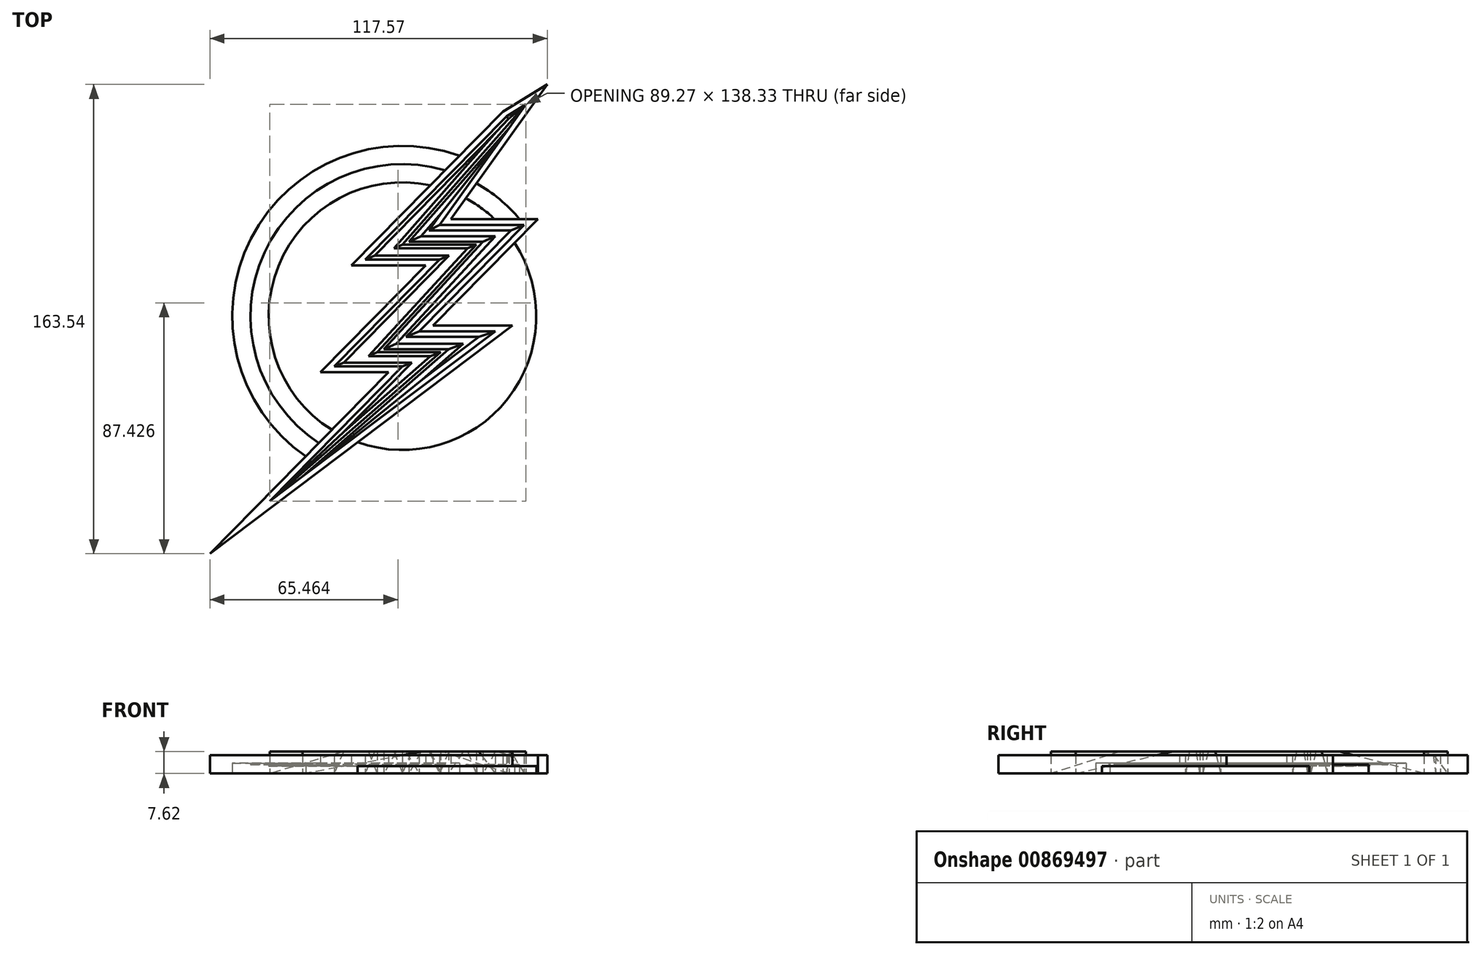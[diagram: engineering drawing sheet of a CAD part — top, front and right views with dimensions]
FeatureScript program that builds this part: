
annotation { "Feature Type Name" : "Feature", "Feature Type Description" : "" }
export const myFeature = defineFeature(function(context is Context, id is Id, definition is map)
    precondition{}
    {
        {
            var Q0;
            Q0=qCreatedBy(makeId("Top.planeOp"),FACE);
            var sketch = newSketch(context, id + "F0", { "sketchPlane" : qUnion([Q0])});
            skCircle(sketch, "E0", {"center": v(0, 0) * mm, "radius": 46.64 * mm});
            skCircle(sketch, "E1.0", {"center": v(0, 0) * mm, "radius": 53 * mm});
            skCircle(sketch, "E2.0", {"center": v(0, 0) * mm, "radius": 59.34 * mm});
            skLineSegment(sketch, "E3", {"start": v(36.25, 69.68) * mm, "end": v(-12.96, 19.72) * mm});
            skLineSegment(sketch, "E4", {"start": v(-12.96, 19.72) * mm, "end": v(12.96, 19.72) * mm});
            skLineSegment(sketch, "E5", {"start": v(12.96, 19.72) * mm, "end": v(-23.75, -17.55) * mm});
            skLineSegment(sketch, "E6", {"start": v(-23.75, -17.55) * mm, "end": v(0, -17.55) * mm});
            skLineSegment(sketch, "E7", {"start": v(0, -17.55) * mm, "end": v(-46.26, -64.52) * mm});
            skLineSegment(sketch, "E8", {"start": v(-46.26, -64.52) * mm, "end": v(24.6, -11.08) * mm});
            skLineSegment(sketch, "E9", {"start": v(24.6, -11.08) * mm, "end": v(32.28, -5.3) * mm});
            skLineSegment(sketch, "E10", {"start": v(32.28, -5.3) * mm, "end": v(5.82, -5.3) * mm});
            skLineSegment(sketch, "E11", {"start": v(5.82, -5.3) * mm, "end": v(37.86, 27.24) * mm});
            skLineSegment(sketch, "E12", {"start": v(37.86, 27.24) * mm, "end": v(42.38, 31.82) * mm});
            skLineSegment(sketch, "E13", {"start": v(42.38, 31.82) * mm, "end": v(12.96, 31.82) * mm});
            skLineSegment(sketch, "E14", {"start": v(12.96, 31.82) * mm, "end": v(43.01, 73.81) * mm});
            skLineSegment(sketch, "E15", {"start": v(43.01, 73.81) * mm, "end": v(36.25, 69.68) * mm});
            skLineSegment(sketch, "E16", {"start": v(-46.26, -64.52) * mm, "end": v(13.33, -12.58) * mm});
            skLineSegment(sketch, "E17", {"start": v(13.33, -12.58) * mm, "end": v(-8.83, -12.58) * mm});
            skLineSegment(sketch, "E18", {"start": v(-8.83, -12.58) * mm, "end": v(25.73, 24.98) * mm});
            skLineSegment(sketch, "E19", {"start": v(25.73, 24.98) * mm, "end": v(0, 24.98) * mm});
            skLineSegment(sketch, "E20", {"start": v(0, 24.98) * mm, "end": v(43.01, 73.81) * mm});
            skLineSegment(sketch, "E21", {"start": v(13.33, -12.58) * mm, "end": v(32.28, -5.3) * mm});
            skLineSegment(sketch, "E22", {"start": v(-8.83, -12.58) * mm, "end": v(-23.75, -17.55) * mm});
            skLineSegment(sketch, "E23", {"start": v(13.33, -12.58) * mm, "end": v(0, -17.55) * mm});
            skLineSegment(sketch, "E24", {"start": v(25.73, 24.98) * mm, "end": v(12.96, 19.72) * mm});
            skLineSegment(sketch, "E25", {"start": v(25.73, 24.98) * mm, "end": v(42.38, 31.82) * mm});
            skLineSegment(sketch, "E26", {"start": v(12.96, 31.82) * mm, "end": v(0, 24.98) * mm});
            skLineSegment(sketch, "E27", {"start": v(0, 24.98) * mm, "end": v(-12.96, 19.72) * mm});
            skLineSegment(sketch, "E28.0", {"start": v(50.48, 80.76) * mm, "end": v(34.98, 71.28) * mm});
            skLineSegment(sketch, "E28.1", {"start": v(16.91, 33.85) * mm, "end": v(50.48, 80.76) * mm});
            skLineSegment(sketch, "E28.2", {"start": v(-4.85, -19.59) * mm, "end": v(-67.1, -82.78) * mm});
            skLineSegment(sketch, "E28.3", {"start": v(-28.6, -19.59) * mm, "end": v(-4.85, -19.59) * mm});
            skLineSegment(sketch, "E28.4", {"start": v(8.1, 17.69) * mm, "end": v(-28.6, -19.59) * mm});
            skLineSegment(sketch, "E28.5", {"start": v(-17.81, 17.69) * mm, "end": v(8.1, 17.69) * mm});
            skLineSegment(sketch, "E28.6", {"start": v(-67.1, -82.78) * mm, "end": v(25.83, -12.7) * mm});
            skLineSegment(sketch, "E28.7", {"start": v(25.83, -12.7) * mm, "end": v(38.35, -3.26) * mm});
            skLineSegment(sketch, "E28.8", {"start": v(34.98, 71.28) * mm, "end": v(-17.81, 17.69) * mm});
            skLineSegment(sketch, "E28.9", {"start": v(38.35, -3.26) * mm, "end": v(10.68, -3.26) * mm});
            skLineSegment(sketch, "E28.10", {"start": v(10.68, -3.26) * mm, "end": v(39.31, 25.81) * mm});
            skLineSegment(sketch, "E28.11", {"start": v(39.31, 25.81) * mm, "end": v(47.23, 33.85) * mm});
            skLineSegment(sketch, "E28.12", {"start": v(47.23, 33.85) * mm, "end": v(16.91, 33.85) * mm});
            skLineSegment(sketch, "E29.0", {"start": v(2.25, 26) * mm, "end": v(43.77, 73.14) * mm});
            skLineSegment(sketch, "E29.1", {"start": v(-45.6, -65.29) * mm, "end": v(16.05, -11.57) * mm});
            skLineSegment(sketch, "E29.2", {"start": v(16.05, -11.57) * mm, "end": v(-6.51, -11.57) * mm});
            skLineSegment(sketch, "E29.3", {"start": v(-6.51, -11.57) * mm, "end": v(28.05, 26) * mm});
            skLineSegment(sketch, "E29.4", {"start": v(28.05, 26) * mm, "end": v(2.25, 26) * mm});
            skSolve(sketch);
        }
        {
            var Q0;
            {var subQ0=sQuery(id+"F0.wireOp",EDGE,"E9");Q0=makeQuery(id+"F0.imprint","IMPRINT",FACE,{"disambiguationData":[TD([[makeQuery(id+"F0.imprint","IMPRINT",EDGE,{"derivedFrom":subQ0}),-1.0]])]});}
            var Q1;
            {var subQ0=sQuery(id+"F0.wireOp",EDGE,"E4");Q1=makeQuery(id+"F0.imprint","IMPRINT",FACE,{"disambiguationData":[TD([[makeQuery(id+"F0.imprint","IMPRINT",EDGE,{"derivedFrom":subQ0}),-1.0]])]});}
            var Q2;
            {var subQ0=sQuery(id+"F0.wireOp",EDGE,"E13");var subQ1=sQuery(id+"F0.wireOp",EDGE,"E0");var subQ2=makeQuery(id+"F0.imprint","INTERSECT",VERTEX,{"derivedFrom":[subQ1,subQ0]});Q2=makeQuery(id+"F0.imprint","IMPRINT",FACE,{"disambiguationData":[TD([[makeQuery(id+"F0.imprint","IMPRINT",EDGE,{"disambiguationData":[TD([[subQ2,-1.0]])],"derivedFrom":subQ1}),1.0]])]});}
            extrude(context, id + "F1", {"entities" : qUnion([Q0, Q1, Q2]), "depth" : 5.08 * mm, "offsetDistance" : 25.4 * mm});
        }
        {
            var Q0;
            {var subQ11=sQuery(id+"F0.wireOp",EDGE,"E4");Q0=makeQuery(id+"F0.imprint","IMPRINT",FACE,{"disambiguationData":[TD([[makeQuery(id+"F0.imprint","IMPRINT",EDGE,{"derivedFrom":subQ11}),-1.0]])]});}
            var Q1;
            {var subQ0=sQuery(id+"F0.wireOp",EDGE,"E9");Q1=makeQuery(id+"F0.imprint","IMPRINT",FACE,{"disambiguationData":[TD([[makeQuery(id+"F0.imprint","IMPRINT",EDGE,{"derivedFrom":subQ0}),-1.0]])]});}
            var Q2;
            {var subQ0=sQuery(id+"F0.wireOp",EDGE,"E8");var subQ1=sQuery(id+"F0.wireOp",EDGE,"E0");var subQ2=makeQuery(id+"F0.imprint","INTERSECT",VERTEX,{"derivedFrom":[subQ1,subQ0]});Q2=makeQuery(id+"F0.imprint","IMPRINT",FACE,{"disambiguationData":[TD([[makeQuery(id+"F0.imprint","IMPRINT",EDGE,{"disambiguationData":[TD([[subQ2,-1.0]])],"derivedFrom":subQ1}),-1.0]])]});}
            var Q3;
            {var subQ0=sQuery(id+"F0.wireOp",EDGE,"E28.2");var subQ1=sQuery(id+"F0.wireOp",EDGE,"E0");var subQ2=makeQuery(id+"F0.imprint","INTERSECT",VERTEX,{"derivedFrom":[subQ1,subQ0]});Q3=makeQuery(id+"F0.imprint","IMPRINT",FACE,{"disambiguationData":[TD([[makeQuery(id+"F0.imprint","IMPRINT",EDGE,{"disambiguationData":[TD([[subQ2,-1.0]])],"derivedFrom":subQ1}),-1.0]])]});}
            var Q4;
            {var subQ0=sQuery(id+"F0.wireOp",EDGE,"E28.2");var subQ1=sQuery(id+"F0.wireOp",EDGE,"E1.0");var subQ2=makeQuery(id+"F0.imprint","INTERSECT",VERTEX,{"derivedFrom":[subQ1,subQ0]});Q4=makeQuery(id+"F0.imprint","IMPRINT",FACE,{"disambiguationData":[TD([[makeQuery(id+"F0.imprint","IMPRINT",EDGE,{"disambiguationData":[TD([[subQ2,-1.0]])],"derivedFrom":subQ1}),-1.0]])]});}
            var Q5;
            {var subQ0=sQuery(id+"F0.wireOp",EDGE,"E8");var subQ1=sQuery(id+"F0.wireOp",EDGE,"E1.0");var subQ2=makeQuery(id+"F0.imprint","INTERSECT",VERTEX,{"derivedFrom":[subQ1,subQ0]});Q5=makeQuery(id+"F0.imprint","IMPRINT",FACE,{"disambiguationData":[TD([[makeQuery(id+"F0.imprint","IMPRINT",EDGE,{"disambiguationData":[TD([[subQ2,-1.0]])],"derivedFrom":subQ1}),-1.0]])]});}
            var Q6;
            {var subQ1=sQuery(id+"F0.wireOp",EDGE,"E7");var subQ3=sQuery(id+"F0.wireOp",EDGE,"E2.0");var subQ5=makeQuery(id+"F0.imprint","INTERSECT",VERTEX,{"derivedFrom":[subQ3,subQ1]});Q6=makeQuery(id+"F0.imprint","IMPRINT",FACE,{"disambiguationData":[TD([[makeQuery(id+"F0.imprint","IMPRINT",EDGE,{"disambiguationData":[TD([[subQ5,1.0]])],"derivedFrom":subQ3}),-1.0]])]});}
            var Q7;
            {var subQ5=sQuery(id+"F0.wireOp",EDGE,"E12");Q7=makeQuery(id+"F0.imprint","IMPRINT",FACE,{"disambiguationData":[TD([[makeQuery(id+"F0.imprint","IMPRINT",EDGE,{"derivedFrom":subQ5}),-1.0]])]});}
            var Q8;
            {var subQ2=sQuery(id+"F0.wireOp",EDGE,"E28.11");var subQ4=sQuery(id+"F0.wireOp",EDGE,"E28.12");var subQ6=makeQuery(id+"F0.imprint","INTERSECT",VERTEX,{"derivedFrom":[subQ2,subQ4]});Q8=makeQuery(id+"F0.imprint","IMPRINT",FACE,{"disambiguationData":[TD([[makeQuery(id+"F0.imprint","IMPRINT",EDGE,{"disambiguationData":[TD([[subQ6,1.0]])],"derivedFrom":subQ2}),1.0]])]});}
            var Q9;
            {var subQ0=sQuery(id+"F0.wireOp",EDGE,"E13");var subQ1=sQuery(id+"F0.wireOp",EDGE,"E0");var subQ2=makeQuery(id+"F0.imprint","INTERSECT",VERTEX,{"derivedFrom":[subQ1,subQ0]});Q9=makeQuery(id+"F0.imprint","IMPRINT",FACE,{"disambiguationData":[TD([[makeQuery(id+"F0.imprint","IMPRINT",EDGE,{"disambiguationData":[TD([[subQ2,-1.0]])],"derivedFrom":subQ1}),-1.0]])]});}
            var Q10;
            {var subQ1=sQuery(id+"F0.wireOp",EDGE,"E13");var subQ3=sQuery(id+"F0.wireOp",EDGE,"E0");var subQ7=makeQuery(id+"F0.imprint","INTERSECT",VERTEX,{"derivedFrom":[subQ3,subQ1]});Q10=makeQuery(id+"F0.imprint","IMPRINT",FACE,{"disambiguationData":[TD([[makeQuery(id+"F0.imprint","IMPRINT",EDGE,{"disambiguationData":[TD([[subQ7,-1.0]])],"derivedFrom":subQ3}),1.0]])]});}
            var Q11;
            {var subQ0=sQuery(id+"F0.wireOp",EDGE,"E28.1");var subQ1=sQuery(id+"F0.wireOp",EDGE,"E0");var subQ2=makeQuery(id+"F0.imprint","INTERSECT",VERTEX,{"derivedFrom":[subQ1,subQ0]});Q11=makeQuery(id+"F0.imprint","IMPRINT",FACE,{"disambiguationData":[TD([[makeQuery(id+"F0.imprint","IMPRINT",EDGE,{"disambiguationData":[TD([[subQ2,-1.0]])],"derivedFrom":subQ1}),-1.0]])]});}
            var Q12;
            {var subQ0=sQuery(id+"F0.wireOp",EDGE,"E28.1");var subQ1=sQuery(id+"F0.wireOp",EDGE,"E1.0");var subQ2=makeQuery(id+"F0.imprint","INTERSECT",VERTEX,{"derivedFrom":[subQ1,subQ0]});Q12=makeQuery(id+"F0.imprint","IMPRINT",FACE,{"disambiguationData":[TD([[makeQuery(id+"F0.imprint","IMPRINT",EDGE,{"disambiguationData":[TD([[subQ2,-1.0]])],"derivedFrom":subQ1}),-1.0]])]});}
            var Q13;
            {var subQ3=sQuery(id+"F0.wireOp",EDGE,"E15");Q13=makeQuery(id+"F0.imprint","IMPRINT",FACE,{"disambiguationData":[TD([[makeQuery(id+"F0.imprint","IMPRINT",EDGE,{"derivedFrom":subQ3}),-1.0]])]});}
            var Q14;
            {var subQ0=sQuery(id+"F0.wireOp",EDGE,"E3");var subQ1=sQuery(id+"F0.wireOp",EDGE,"E1.0");var subQ2=makeQuery(id+"F0.imprint","INTERSECT",VERTEX,{"derivedFrom":[subQ1,subQ0]});Q14=makeQuery(id+"F0.imprint","IMPRINT",FACE,{"disambiguationData":[TD([[makeQuery(id+"F0.imprint","IMPRINT",EDGE,{"disambiguationData":[TD([[subQ2,-1.0]])],"derivedFrom":subQ1}),-1.0]])]});}
            var Q15;
            {var subQ0=sQuery(id+"F0.wireOp",EDGE,"E3");var subQ1=sQuery(id+"F0.wireOp",EDGE,"E0");var subQ2=makeQuery(id+"F0.imprint","INTERSECT",VERTEX,{"derivedFrom":[subQ1,subQ0]});Q15=makeQuery(id+"F0.imprint","IMPRINT",FACE,{"disambiguationData":[TD([[makeQuery(id+"F0.imprint","IMPRINT",EDGE,{"disambiguationData":[TD([[subQ2,-1.0]])],"derivedFrom":subQ1}),-1.0]])]});}
            extrude(context, id + "F2", {"entities" : qUnion([Q0, Q1, Q2, Q3, Q4, Q5, Q6, Q7, Q8, Q9, Q10, Q11, Q12, Q13, Q14, Q15]), "depth" : 6.35 * mm, "offsetDistance" : 25.4 * mm});
        }
        {
            var Q0;
            {var subQ1=sQuery(id+"F0.wireOp",EDGE,"E0");var subQ6=sQuery(id+"F0.wireOp",EDGE,"E16");var subQ9=makeQuery(id+"F0.imprint","INTERSECT",VERTEX,{"derivedFrom":[subQ1,subQ6]});Q0=makeQuery(id+"F0.imprint","IMPRINT",FACE,{"disambiguationData":[TD([[makeQuery(id+"F0.imprint","IMPRINT",EDGE,{"disambiguationData":[TD([[subQ9,-1.0]])],"derivedFrom":subQ1}),1.0]])]});}
            var Q1;
            {var subQ7=sQuery(id+"F0.wireOp",EDGE,"E17");Q1=makeQuery(id+"F0.imprint","IMPRINT",FACE,{"disambiguationData":[TD([[makeQuery(id+"F0.imprint","IMPRINT",EDGE,{"derivedFrom":subQ7}),-1.0]])]});}
            var Q2;
            {var subQ4=sQuery(id+"F0.wireOp",EDGE,"E19");Q2=makeQuery(id+"F0.imprint","IMPRINT",FACE,{"disambiguationData":[TD([[makeQuery(id+"F0.imprint","IMPRINT",EDGE,{"derivedFrom":subQ4}),-1.0]])]});}
            var Q3;
            {var subQ0=sQuery(id+"F0.wireOp",EDGE,"E29.0");var subQ1=sQuery(id+"F0.wireOp",EDGE,"E0");var subQ2=makeQuery(id+"F0.imprint","INTERSECT",VERTEX,{"derivedFrom":[subQ1,subQ0]});Q3=makeQuery(id+"F0.imprint","IMPRINT",FACE,{"disambiguationData":[TD([[makeQuery(id+"F0.imprint","IMPRINT",EDGE,{"disambiguationData":[TD([[subQ2,-1.0]])],"derivedFrom":subQ1}),1.0]])]});}
            var Q4;
            {var subQ0=sQuery(id+"F0.wireOp",EDGE,"E29.0");var subQ1=sQuery(id+"F0.wireOp",EDGE,"E0");var subQ2=makeQuery(id+"F0.imprint","INTERSECT",VERTEX,{"derivedFrom":[subQ1,subQ0]});Q4=makeQuery(id+"F0.imprint","IMPRINT",FACE,{"disambiguationData":[TD([[makeQuery(id+"F0.imprint","IMPRINT",EDGE,{"disambiguationData":[TD([[subQ2,-1.0]])],"derivedFrom":subQ1}),-1.0]])]});}
            var Q5;
            {var subQ0=sQuery(id+"F0.wireOp",EDGE,"E29.0");var subQ1=sQuery(id+"F0.wireOp",EDGE,"E1.0");var subQ2=makeQuery(id+"F0.imprint","INTERSECT",VERTEX,{"derivedFrom":[subQ1,subQ0]});Q5=makeQuery(id+"F0.imprint","IMPRINT",FACE,{"disambiguationData":[TD([[makeQuery(id+"F0.imprint","IMPRINT",EDGE,{"disambiguationData":[TD([[subQ2,-1.0]])],"derivedFrom":subQ1}),-1.0]])]});}
            var Q6;
            {var subQ0=sQuery(id+"F0.wireOp",EDGE,"E20");var subQ1=sQuery(id+"F0.wireOp",EDGE,"E2.0");var subQ2=makeQuery(id+"F0.imprint","INTERSECT",VERTEX,{"derivedFrom":[subQ1,subQ0]});Q6=makeQuery(id+"F0.imprint","IMPRINT",FACE,{"disambiguationData":[TD([[makeQuery(id+"F0.imprint","IMPRINT",EDGE,{"disambiguationData":[TD([[subQ2,1.0]])],"derivedFrom":subQ1}),-1.0]])]});}
            var Q7;
            {var subQ0=sQuery(id+"F0.wireOp",EDGE,"E16");var subQ1=sQuery(id+"F0.wireOp",EDGE,"E0");var subQ2=makeQuery(id+"F0.imprint","INTERSECT",VERTEX,{"derivedFrom":[subQ1,subQ0]});Q7=makeQuery(id+"F0.imprint","IMPRINT",FACE,{"disambiguationData":[TD([[makeQuery(id+"F0.imprint","IMPRINT",EDGE,{"disambiguationData":[TD([[subQ2,-1.0]])],"derivedFrom":subQ1}),-1.0]])]});}
            var Q8;
            {var subQ0=sQuery(id+"F0.wireOp",EDGE,"E16");var subQ1=sQuery(id+"F0.wireOp",EDGE,"E1.0");var subQ2=makeQuery(id+"F0.imprint","INTERSECT",VERTEX,{"derivedFrom":[subQ1,subQ0]});Q8=makeQuery(id+"F0.imprint","IMPRINT",FACE,{"disambiguationData":[TD([[makeQuery(id+"F0.imprint","IMPRINT",EDGE,{"disambiguationData":[TD([[subQ2,-1.0]])],"derivedFrom":subQ1}),-1.0]])]});}
            var Q9;
            {var subQ0=sQuery(id+"F0.wireOp",EDGE,"E16");var subQ1=sQuery(id+"F0.wireOp",EDGE,"E2.0");var subQ2=makeQuery(id+"F0.imprint","INTERSECT",VERTEX,{"derivedFrom":[subQ1,subQ0]});Q9=makeQuery(id+"F0.imprint","IMPRINT",FACE,{"disambiguationData":[TD([[makeQuery(id+"F0.imprint","IMPRINT",EDGE,{"disambiguationData":[TD([[subQ2,-1.0]])],"derivedFrom":subQ1}),-1.0]])]});}
            extrude(context, id + "F3", {"entities" : qUnion([Q0, Q1, Q2, Q3, Q4, Q5, Q6, Q7, Q8, Q9]), "operationType" : NewBodyOperationType.ADD, "depth" : 7.62 * mm, "offsetDistance" : 25.4 * mm});
        }
        {
            var Q0;
            {var subQ1=sQuery(id+"F0.wireOp",EDGE,"E10");Q0=makeQuery(id+"F0.imprint","IMPRINT",FACE,{"disambiguationData":[TD([[makeQuery(id+"F0.imprint","IMPRINT",EDGE,{"derivedFrom":subQ1}),1.0]])]});}
            var Q1;
            {var subQ0=sQuery(id+"F0.wireOp",EDGE,"E9");Q1=makeQuery(id+"F0.imprint","IMPRINT",FACE,{"disambiguationData":[TD([[makeQuery(id+"F0.imprint","IMPRINT",EDGE,{"derivedFrom":subQ0}),1.0]])]});}
            var Q2;
            {var subQ11=sQuery(id+"F0.wireOp",EDGE,"E29.4");Q2=makeQuery(id+"F0.imprint","IMPRINT",FACE,{"disambiguationData":[TD([[makeQuery(id+"F0.imprint","IMPRINT",EDGE,{"derivedFrom":subQ11}),-1.0]])]});}
            var Q3;
            {var subQ0=sQuery(id+"F0.wireOp",EDGE,"E14");var subQ1=sQuery(id+"F0.wireOp",EDGE,"E0");var subQ2=makeQuery(id+"F0.imprint","INTERSECT",VERTEX,{"derivedFrom":[subQ1,subQ0]});Q3=makeQuery(id+"F0.imprint","IMPRINT",FACE,{"disambiguationData":[TD([[makeQuery(id+"F0.imprint","IMPRINT",EDGE,{"disambiguationData":[TD([[subQ2,-1.0]])],"derivedFrom":subQ1}),1.0]])]});}
            var Q4;
            {var subQ0=sQuery(id+"F0.wireOp",EDGE,"E14");var subQ1=sQuery(id+"F0.wireOp",EDGE,"E0");var subQ2=makeQuery(id+"F0.imprint","INTERSECT",VERTEX,{"derivedFrom":[subQ1,subQ0]});Q4=makeQuery(id+"F0.imprint","IMPRINT",FACE,{"disambiguationData":[TD([[makeQuery(id+"F0.imprint","IMPRINT",EDGE,{"disambiguationData":[TD([[subQ2,-1.0]])],"derivedFrom":subQ1}),-1.0]])]});}
            var Q5;
            {var subQ0=sQuery(id+"F0.wireOp",EDGE,"E14");var subQ1=sQuery(id+"F0.wireOp",EDGE,"E1.0");var subQ2=makeQuery(id+"F0.imprint","INTERSECT",VERTEX,{"derivedFrom":[subQ1,subQ0]});Q5=makeQuery(id+"F0.imprint","IMPRINT",FACE,{"disambiguationData":[TD([[makeQuery(id+"F0.imprint","IMPRINT",EDGE,{"disambiguationData":[TD([[subQ2,-1.0]])],"derivedFrom":subQ1}),-1.0]])]});}
            var Q6;
            {var subQ0=sQuery(id+"F0.wireOp",EDGE,"E14");var subQ1=sQuery(id+"F0.wireOp",EDGE,"E2.0");var subQ2=makeQuery(id+"F0.imprint","INTERSECT",VERTEX,{"derivedFrom":[subQ1,subQ0]});Q6=makeQuery(id+"F0.imprint","IMPRINT",FACE,{"disambiguationData":[TD([[makeQuery(id+"F0.imprint","IMPRINT",EDGE,{"disambiguationData":[TD([[subQ2,-1.0]])],"derivedFrom":subQ1}),-1.0]])]});}
            var Q7;
            {var subQ0=sQuery(id+"F0.wireOp",EDGE,"E12");Q7=makeQuery(id+"F0.imprint","IMPRINT",FACE,{"disambiguationData":[TD([[makeQuery(id+"F0.imprint","IMPRINT",EDGE,{"derivedFrom":subQ0}),1.0]])]});}
            var Q8;
            {var subQ0=sQuery(id+"F0.wireOp",EDGE,"E13");var subQ1=sQuery(id+"F0.wireOp",EDGE,"E0");var subQ2=makeQuery(id+"F0.imprint","INTERSECT",VERTEX,{"derivedFrom":[subQ1,subQ0]});Q8=makeQuery(id+"F0.imprint","IMPRINT",FACE,{"disambiguationData":[TD([[makeQuery(id+"F0.imprint","IMPRINT",EDGE,{"disambiguationData":[TD([[subQ2,1.0]])],"derivedFrom":subQ1}),-1.0]])]});}
            var Q9;
            {var subQ0=sQuery(id+"F0.wireOp",EDGE,"E8");var subQ1=sQuery(id+"F0.wireOp",EDGE,"E0");var subQ2=makeQuery(id+"F0.imprint","INTERSECT",VERTEX,{"derivedFrom":[subQ1,subQ0]});Q9=makeQuery(id+"F0.imprint","IMPRINT",FACE,{"disambiguationData":[TD([[makeQuery(id+"F0.imprint","IMPRINT",EDGE,{"disambiguationData":[TD([[subQ2,1.0]])],"derivedFrom":subQ1}),-1.0]])]});}
            var Q10;
            {var subQ0=sQuery(id+"F0.wireOp",EDGE,"E29.1");var subQ1=sQuery(id+"F0.wireOp",EDGE,"E1.0");var subQ2=makeQuery(id+"F0.imprint","INTERSECT",VERTEX,{"derivedFrom":[subQ1,subQ0]});Q10=makeQuery(id+"F0.imprint","IMPRINT",FACE,{"disambiguationData":[TD([[makeQuery(id+"F0.imprint","IMPRINT",EDGE,{"disambiguationData":[TD([[subQ2,-1.0]])],"derivedFrom":subQ1}),-1.0]])]});}
            var Q11;
            {var subQ0=sQuery(id+"F0.wireOp",EDGE,"E8");var subQ1=sQuery(id+"F0.wireOp",EDGE,"E2.0");var subQ2=makeQuery(id+"F0.imprint","INTERSECT",VERTEX,{"derivedFrom":[subQ1,subQ0]});Q11=makeQuery(id+"F0.imprint","IMPRINT",FACE,{"disambiguationData":[TD([[makeQuery(id+"F0.imprint","IMPRINT",EDGE,{"disambiguationData":[TD([[subQ2,1.0]])],"derivedFrom":subQ1}),-1.0]])]});}
            var Q12;
            Q12=makeQuery(id+"F3.opExtrude","CAP_FACE",FACE,{"disambiguationData":[OSD([sQuery(id+"F0.wireOp",EDGE,"E8"),sQuery(id+"F0.wireOp",EDGE,"E14"),sQuery(id+"F0.wireOp",EDGE,"E16"),sQuery(id+"F0.wireOp",EDGE,"E17"),sQuery(id+"F0.wireOp",EDGE,"E18"),sQuery(id+"F0.wireOp",EDGE,"E19"),sQuery(id+"F0.wireOp",EDGE,"E20"),sQuery(id+"F0.wireOp",EDGE,"E29.0"),sQuery(id+"F0.wireOp",EDGE,"E29.1"),sQuery(id+"F0.wireOp",EDGE,"E29.2"),sQuery(id+"F0.wireOp",EDGE,"E29.3"),sQuery(id+"F0.wireOp",EDGE,"E29.4")])],"isStart":false});
            extrude(context, id + "F4", {"entities" : qUnion([Q0, Q1, Q2, Q3, Q4, Q5, Q6, Q7, Q8, Q9, Q10, Q11]), "operationType" : NewBodyOperationType.ADD, "endBound" : BoundingType.UP_TO_SURFACE, "depth" : 25.4 * mm, "endBoundEntityFace" : qUnion([Q12]), "offsetDistance" : 25.4 * mm, "hasDraft" : true, "draftAngle" : 14 * degree, "draftPullDirection" : true});
        }
        {
            var Q0;
            Q0=makeQuery(id+"F0.imprint","IMPRINT",FACE,{"disambiguationData":[TD([[makeQuery(id+"F0.imprint","IMPRINT",EDGE,{"derivedFrom":sQuery(id+"F0.wireOp",EDGE,"E5")}),1.0]])]});
            var Q1;
            Q1=makeQuery(id+"F0.imprint","IMPRINT",FACE,{"disambiguationData":[TD([[makeQuery(id+"F0.imprint","IMPRINT",EDGE,{"derivedFrom":sQuery(id+"F0.wireOp",EDGE,"E4")}),1.0]])]});
            var Q2;
            {var subQ5=sQuery(id+"F0.wireOp",EDGE,"E27");Q2=makeQuery(id+"F0.imprint","IMPRINT",FACE,{"disambiguationData":[TD([[makeQuery(id+"F0.imprint","IMPRINT",EDGE,{"derivedFrom":subQ5}),-1.0]])]});}
            var Q3;
            {var subQ0=sQuery(id+"F0.wireOp",EDGE,"E3");var subQ1=sQuery(id+"F0.wireOp",EDGE,"E0");var subQ2=makeQuery(id+"F0.imprint","INTERSECT",VERTEX,{"derivedFrom":[subQ1,subQ0]});Q3=makeQuery(id+"F0.imprint","IMPRINT",FACE,{"disambiguationData":[TD([[makeQuery(id+"F0.imprint","IMPRINT",EDGE,{"disambiguationData":[TD([[subQ2,1.0]])],"derivedFrom":subQ1}),-1.0]])]});}
            var Q4;
            {var subQ0=sQuery(id+"F0.wireOp",EDGE,"E3");var subQ1=sQuery(id+"F0.wireOp",EDGE,"E1.0");var subQ2=makeQuery(id+"F0.imprint","INTERSECT",VERTEX,{"derivedFrom":[subQ1,subQ0]});Q4=makeQuery(id+"F0.imprint","IMPRINT",FACE,{"disambiguationData":[TD([[makeQuery(id+"F0.imprint","IMPRINT",EDGE,{"disambiguationData":[TD([[subQ2,1.0]])],"derivedFrom":subQ1}),-1.0]])]});}
            var Q5;
            {var subQ5=sQuery(id+"F0.wireOp",EDGE,"E15");Q5=makeQuery(id+"F0.imprint","IMPRINT",FACE,{"disambiguationData":[TD([[makeQuery(id+"F0.imprint","IMPRINT",EDGE,{"derivedFrom":subQ5}),1.0]])]});}
            var Q6;
            Q6=makeQuery(id+"F0.imprint","IMPRINT",FACE,{"disambiguationData":[TD([[makeQuery(id+"F0.imprint","IMPRINT",EDGE,{"derivedFrom":sQuery(id+"F0.wireOp",EDGE,"E6")}),1.0]])]});
            var Q7;
            {var subQ5=sQuery(id+"F0.wireOp",EDGE,"E23");Q7=makeQuery(id+"F0.imprint","IMPRINT",FACE,{"disambiguationData":[TD([[makeQuery(id+"F0.imprint","IMPRINT",EDGE,{"derivedFrom":subQ5}),1.0]])]});}
            var Q8;
            {var subQ0=sQuery(id+"F0.wireOp",EDGE,"E16");var subQ1=sQuery(id+"F0.wireOp",EDGE,"E0");var subQ2=makeQuery(id+"F0.imprint","INTERSECT",VERTEX,{"derivedFrom":[subQ1,subQ0]});Q8=makeQuery(id+"F0.imprint","IMPRINT",FACE,{"disambiguationData":[TD([[makeQuery(id+"F0.imprint","IMPRINT",EDGE,{"disambiguationData":[TD([[subQ2,1.0]])],"derivedFrom":subQ1}),-1.0]])]});}
            var Q9;
            {var subQ0=sQuery(id+"F0.wireOp",EDGE,"E16");var subQ1=sQuery(id+"F0.wireOp",EDGE,"E1.0");var subQ2=makeQuery(id+"F0.imprint","INTERSECT",VERTEX,{"derivedFrom":[subQ1,subQ0]});Q9=makeQuery(id+"F0.imprint","IMPRINT",FACE,{"disambiguationData":[TD([[makeQuery(id+"F0.imprint","IMPRINT",EDGE,{"disambiguationData":[TD([[subQ2,1.0]])],"derivedFrom":subQ1}),-1.0]])]});}
            var Q10;
            {var subQ0=sQuery(id+"F0.wireOp",EDGE,"E7");var subQ1=sQuery(id+"F0.wireOp",EDGE,"E2.0");var subQ2=makeQuery(id+"F0.imprint","INTERSECT",VERTEX,{"derivedFrom":[subQ1,subQ0]});Q10=makeQuery(id+"F0.imprint","IMPRINT",FACE,{"disambiguationData":[TD([[makeQuery(id+"F0.imprint","IMPRINT",EDGE,{"disambiguationData":[TD([[subQ2,-1.0]])],"derivedFrom":subQ1}),-1.0]])]});}
            extrude(context, id + "F5", {"entities" : qUnion([Q0, Q1, Q2, Q3, Q4, Q5, Q6, Q7, Q8, Q9, Q10]), "operationType" : NewBodyOperationType.ADD, "depth" : 7.62 * mm, "offsetDistance" : 25.4 * mm, "hasDraft" : true, "draftAngle" : 10 * degree, "draftPullDirection" : true});
        }
        {
            var Q0;
            {var subQ0=sQuery(id+"F0.wireOp",EDGE,"E28.3");Q0=makeQuery(id+"F0.imprint","IMPRINT",FACE,{"disambiguationData":[TD([[makeQuery(id+"F0.imprint","IMPRINT",EDGE,{"derivedFrom":subQ0}),-1.0]])]});}
            var Q1;
            {var subQ3=sQuery(id+"F0.wireOp",EDGE,"E28.7");Q1=makeQuery(id+"F0.imprint","IMPRINT",FACE,{"disambiguationData":[TD([[makeQuery(id+"F0.imprint","IMPRINT",EDGE,{"derivedFrom":subQ3}),-1.0]])]});}
            var Q2;
            {var subQ0=sQuery(id+"F0.wireOp",EDGE,"E28.12");var subQ1=sQuery(id+"F0.wireOp",EDGE,"E0");var subQ2=makeQuery(id+"F0.imprint","INTERSECT",VERTEX,{"derivedFrom":[subQ1,subQ0]});Q2=makeQuery(id+"F0.imprint","IMPRINT",FACE,{"disambiguationData":[TD([[makeQuery(id+"F0.imprint","IMPRINT",EDGE,{"disambiguationData":[TD([[subQ2,-1.0]])],"derivedFrom":subQ1}),1.0]])]});}
            extrude(context, id + "F6", {"entities" : qUnion([Q0, Q1, Q2]), "operationType" : NewBodyOperationType.ADD, "depth" : 2.54 * mm, "offsetDistance" : 25.4 * mm});
        }
        {
            var Q0;
            {var subQ4=sQuery(id+"F0.wireOp",EDGE,"E0");var subQ5=makeQuery(id+"F0.imprint","IMPRINT",VERTEX,{"derivedFrom":subQ4});Q0=makeQuery(id+"F0.imprint","IMPRINT",FACE,{"disambiguationData":[TD([[makeQuery(id+"F0.imprint","IMPRINT",EDGE,{"disambiguationData":[TD([[subQ5,-1.0]])],"derivedFrom":subQ4}),-1.0]])]});}
            var Q1;
            {var subQ0=sQuery(id+"F0.wireOp",EDGE,"E28.12");var subQ1=sQuery(id+"F0.wireOp",EDGE,"E0");var subQ2=makeQuery(id+"F0.imprint","INTERSECT",VERTEX,{"derivedFrom":[subQ1,subQ0]});Q1=makeQuery(id+"F0.imprint","IMPRINT",FACE,{"disambiguationData":[TD([[makeQuery(id+"F0.imprint","IMPRINT",EDGE,{"disambiguationData":[TD([[subQ2,-1.0]])],"derivedFrom":subQ1}),-1.0]])]});}
            var Q2;
            {var subQ0=sQuery(id+"F0.wireOp",EDGE,"E28.8");var subQ1=sQuery(id+"F0.wireOp",EDGE,"E0");var subQ2=makeQuery(id+"F0.imprint","INTERSECT",VERTEX,{"derivedFrom":[subQ1,subQ0]});Q2=makeQuery(id+"F0.imprint","IMPRINT",FACE,{"disambiguationData":[TD([[makeQuery(id+"F0.imprint","IMPRINT",EDGE,{"disambiguationData":[TD([[subQ2,-1.0]])],"derivedFrom":subQ1}),-1.0]])]});}
            extrude(context, id + "F7", {"entities" : qUnion([Q0, Q1, Q2]), "operationType" : NewBodyOperationType.ADD, "depth" : 3.05 * mm, "offsetDistance" : 25.4 * mm});
        }
        {
            var Q0;
            {var subQ5=sQuery(id+"F0.wireOp",EDGE,"E1.0");var subQ10=makeQuery(id+"F0.imprint","IMPRINT",VERTEX,{"derivedFrom":subQ5});Q0=makeQuery(id+"F0.imprint","IMPRINT",FACE,{"disambiguationData":[TD([[makeQuery(id+"F0.imprint","IMPRINT",EDGE,{"disambiguationData":[TD([[subQ10,-1.0]])],"derivedFrom":subQ5}),-1.0]])]});}
            var Q1;
            {var subQ0=sQuery(id+"F0.wireOp",EDGE,"E28.8");var subQ1=sQuery(id+"F0.wireOp",EDGE,"E1.0");var subQ2=makeQuery(id+"F0.imprint","INTERSECT",VERTEX,{"derivedFrom":[subQ1,subQ0]});Q1=makeQuery(id+"F0.imprint","IMPRINT",FACE,{"disambiguationData":[TD([[makeQuery(id+"F0.imprint","IMPRINT",EDGE,{"disambiguationData":[TD([[subQ2,-1.0]])],"derivedFrom":subQ1}),-1.0]])]});}
            extrude(context, id + "F8", {"entities" : qUnion([Q0, Q1]), "operationType" : NewBodyOperationType.ADD, "depth" : 3.56 * mm, "offsetDistance" : 25.4 * mm});
        }
    });
